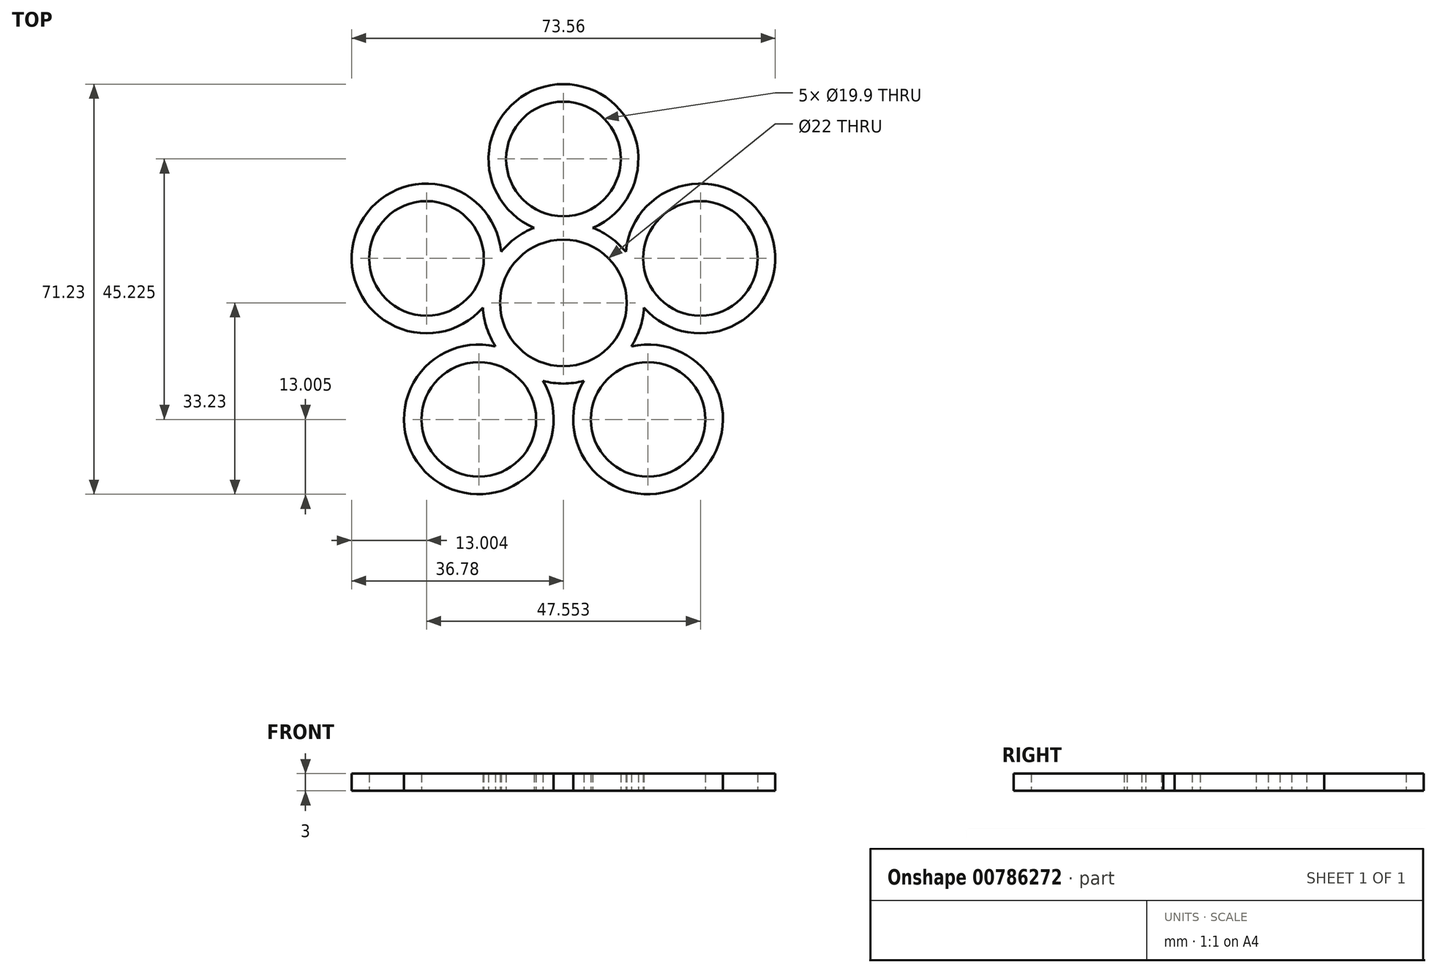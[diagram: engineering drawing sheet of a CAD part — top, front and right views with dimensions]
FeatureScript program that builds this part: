
annotation { "Feature Type Name" : "Feature", "Feature Type Description" : "" }
export const myFeature = defineFeature(function(context is Context, id is Id, definition is map)
    precondition{}
    {
        {
            var Q0;
            Q0=qCreatedBy(makeId("Top.planeOp"),FACE);
            var sketch = newSketch(context, id + "F0", { "sketchPlane" : qUnion([Q0])});
            skArc(sketch, "E0", {"start": v(9.53, 5.5) * mm, "mid": v(0, 11) * mm, "end": v(-9.53, 5.5) * mm});
            skArc(sketch, "E1", {"start": v(12.12, 7) * mm, "mid": v(9.12, 10.62) * mm, "end": v(5.1, 13.04) * mm});
            skCircle(sketch, "E2", {"center": v(0, 25) * mm, "radius": 9.95 * mm});
            skArc(sketch, "E3", {"start": v(5.1, 13.04) * mm, "mid": v(0, 38) * mm, "end": v(-5.1, 13.04) * mm});
            skArc(sketch, "E4.trimOffspring", {"start": v(-5.1, 13.04) * mm, "mid": v(-9.12, 10.62) * mm, "end": v(-12.12, 7) * mm});
            skArc(sketch, "E5.1.0", {"start": v(-10.83, 8.88) * mm, "mid": v(-36.14, 11.74) * mm, "end": v(-13.98, -0.82) * mm});
            skCircle(sketch, "E5.1.1", {"center": v(-23.78, 7.73) * mm, "radius": 9.95 * mm});
            skArc(sketch, "E5.1.2", {"start": v(-2.91, 13.7) * mm, "mid": v(-7.28, 11.96) * mm, "end": v(-10.83, 8.88) * mm});
            skArc(sketch, "E5.1.3", {"start": v(-2.29, 10.76) * mm, "mid": v(-10.46, 3.4) * mm, "end": v(-8.17, -7.36) * mm});
            skArc(sketch, "E5.1.4", {"start": v(-13.98, -0.82) * mm, "mid": v(-12.92, -5.4) * mm, "end": v(-10.4, -9.37) * mm});
            skArc(sketch, "E5.2.0", {"start": v(-11.79, -7.55) * mm, "mid": v(-22.34, -30.74) * mm, "end": v(-3.54, -13.54) * mm});
            skCircle(sketch, "E5.2.1", {"center": v(-14.7, -20.23) * mm, "radius": 9.95 * mm});
            skArc(sketch, "E5.2.2", {"start": v(-13.92, 1.46) * mm, "mid": v(-13.62, -3.23) * mm, "end": v(-11.79, -7.55) * mm});
            skArc(sketch, "E5.2.3", {"start": v(-10.94, 1.15) * mm, "mid": v(-6.47, -8.9) * mm, "end": v(4.47, -10.05) * mm});
            skArc(sketch, "E5.2.4", {"start": v(-3.54, -13.54) * mm, "mid": v(1.14, -13.95) * mm, "end": v(5.7, -12.79) * mm});
            skArc(sketch, "E5.3.0", {"start": v(3.54, -13.54) * mm, "mid": v(22.34, -30.74) * mm, "end": v(11.79, -7.55) * mm});
            skCircle(sketch, "E5.3.1", {"center": v(14.7, -20.23) * mm, "radius": 9.95 * mm});
            skArc(sketch, "E5.3.2", {"start": v(-5.7, -12.79) * mm, "mid": v(-1.14, -13.95) * mm, "end": v(3.54, -13.54) * mm});
            skArc(sketch, "E5.3.3", {"start": v(-4.47, -10.05) * mm, "mid": v(6.47, -8.9) * mm, "end": v(10.94, 1.15) * mm});
            skArc(sketch, "E5.3.4", {"start": v(11.79, -7.55) * mm, "mid": v(13.62, -3.23) * mm, "end": v(13.92, 1.46) * mm});
            skArc(sketch, "E5.4.0", {"start": v(13.98, -0.82) * mm, "mid": v(36.14, 11.74) * mm, "end": v(10.83, 8.88) * mm});
            skCircle(sketch, "E5.4.1", {"center": v(23.78, 7.73) * mm, "radius": 9.95 * mm});
            skArc(sketch, "E5.4.2", {"start": v(10.4, -9.37) * mm, "mid": v(12.92, -5.4) * mm, "end": v(13.98, -0.82) * mm});
            skArc(sketch, "E5.4.3", {"start": v(8.17, -7.36) * mm, "mid": v(10.46, 3.4) * mm, "end": v(2.29, 10.76) * mm});
            skArc(sketch, "E5.4.4", {"start": v(10.83, 8.88) * mm, "mid": v(7.28, 11.96) * mm, "end": v(2.91, 13.7) * mm});
            skSolve(sketch);
        }
        {
            var Q0;
            Q0 = qSketchRegion(id + "F0", true);
            extrude(context, id + "F1", {"entities" : qUnion([Q0]), "depth" : 3 * mm, "offsetDistance" : 25 * mm});
        }
    });
